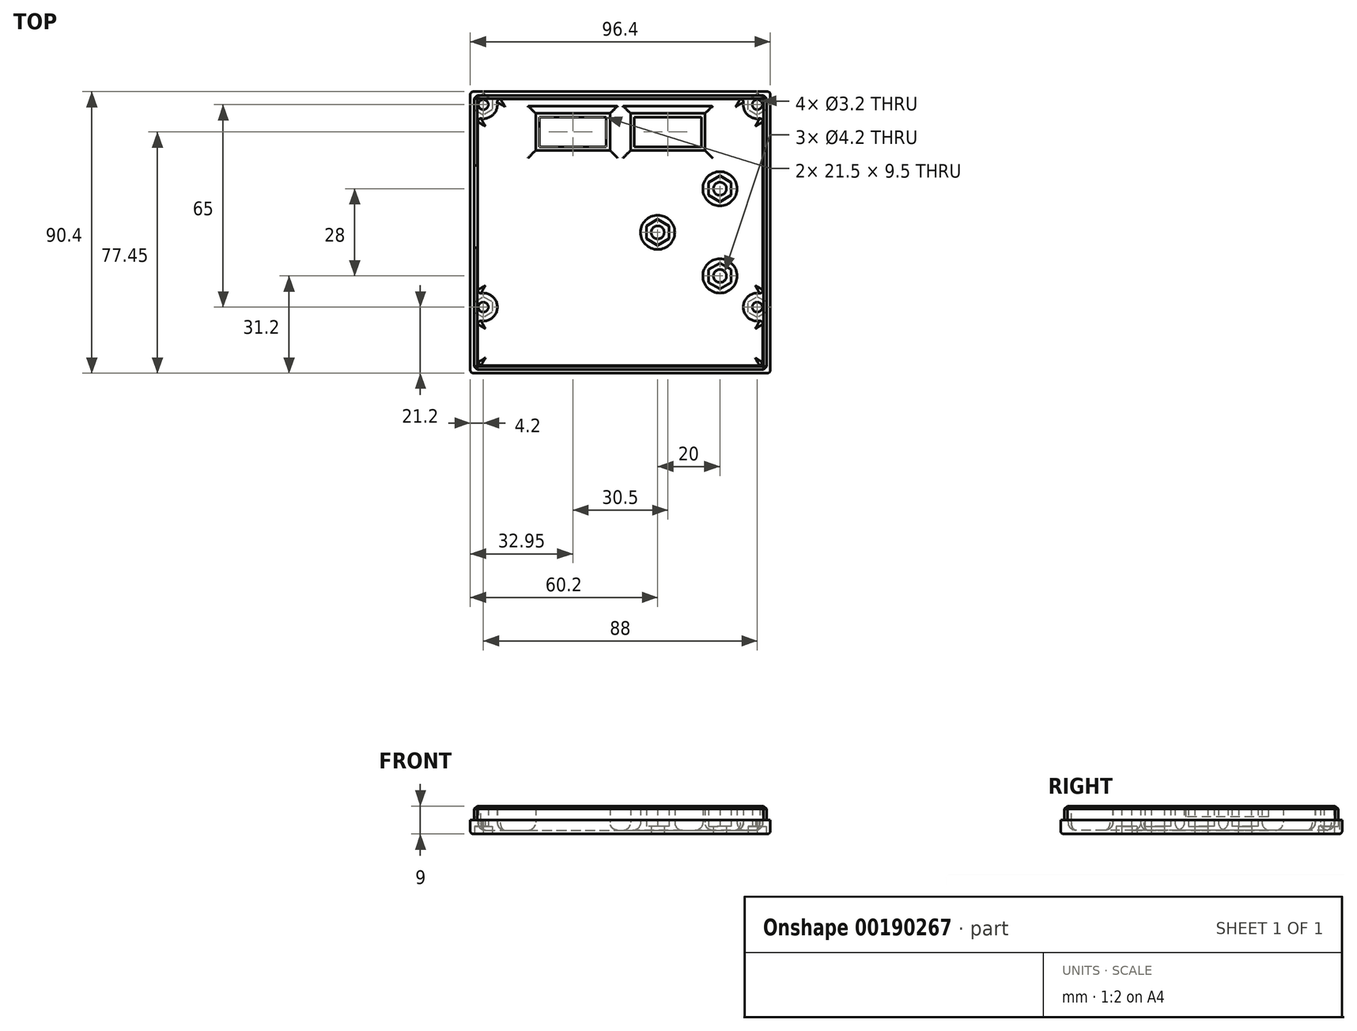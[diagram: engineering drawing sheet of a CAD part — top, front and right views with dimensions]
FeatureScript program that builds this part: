
annotation { "Feature Type Name" : "Feature", "Feature Type Description" : "" }
export const myFeature = defineFeature(function(context is Context, id is Id, definition is map)
    precondition{}
    {
        {
            var Q0;
            Q0=qCreatedBy(makeId("Top.planeOp"),FACE);
            var sketch = newSketch(context, id + "F0", { "sketchPlane" : qUnion([Q0])});
            skLineSegment(sketch, "E0.bottom", {"start": v(-47, 44) * mm, "end": v(47, 44) * mm});
            skLineSegment(sketch, "E0.top", {"start": v(-47, -44) * mm, "end": v(47, -44) * mm});
            skLineSegment(sketch, "E0.left", {"start": v(-47, 44) * mm, "end": v(-47, -44) * mm});
            skLineSegment(sketch, "E0.right", {"start": v(47, 44) * mm, "end": v(47, -44) * mm});
            skLineSegment(sketch, "E1.0", {"start": v(-48.2, 45.2) * mm, "end": v(48.2, 45.2) * mm});
            skLineSegment(sketch, "E1.1", {"start": v(-48.2, 45.2) * mm, "end": v(-48.2, -45.2) * mm});
            skLineSegment(sketch, "E1.2", {"start": v(-48.2, -45.2) * mm, "end": v(48.2, -45.2) * mm});
            skLineSegment(sketch, "E1.3", {"start": v(48.2, 45.2) * mm, "end": v(48.2, -45.2) * mm});
            skCircle(sketch, "E2", {"center": v(-44, 41) * mm, "radius": 1.6 * mm});
            skCircle(sketch, "E3", {"center": v(44, 41) * mm, "radius": 1.6 * mm});
            skCircle(sketch, "E4", {"center": v(-44, -24) * mm, "radius": 1.6 * mm});
            skCircle(sketch, "E5", {"center": v(44, -24) * mm, "radius": 1.6 * mm});
            skArc(sketch, "E6", {"start": v(-44.65, 36.55) * mm, "mid": v(-40.82, 37.82) * mm, "end": v(-39.55, 41.65) * mm});
            skArc(sketch, "E7", {"start": v(39.55, 41.65) * mm, "mid": v(40.82, 37.82) * mm, "end": v(44.65, 36.55) * mm});
            skArc(sketch, "E8", {"start": v(-44.65, -28.45) * mm, "mid": v(-39.5, -24) * mm, "end": v(-44.65, -19.55) * mm});
            skArc(sketch, "E9", {"start": v(44.65, -19.55) * mm, "mid": v(39.5, -24) * mm, "end": v(44.65, -28.45) * mm});
            skLineSegment(sketch, "E10", {"start": v(-48.2, 21.5) * mm, "end": v(-47, 21.5) * mm});
            skLineSegment(sketch, "E11", {"start": v(-48.2, -5) * mm, "end": v(-47, -5) * mm});
            skLineSegment(sketch, "E12.top", {"start": v(-45.8, -42.8) * mm, "end": v(45.8, -42.8) * mm});
            skLineSegment(sketch, "E12.left", {"start": v(-45.8, 35.56) * mm, "end": v(-45.8, -18.56) * mm});
            skLineSegment(sketch, "E12.right", {"start": v(45.8, 35.56) * mm, "end": v(45.8, -18.56) * mm});
            skLineSegment(sketch, "E13.trimOffspring", {"start": v(-45.8, -29.44) * mm, "end": v(-45.8, -42.8) * mm});
            skLineSegment(sketch, "E14.trimOffspring", {"start": v(45.8, -29.44) * mm, "end": v(45.8, -42.8) * mm});
            skArc(sketch, "E15.filletArc", {"start": v(45.8, -29.44) * mm, "mid": v(45.45, -28.68) * mm, "end": v(44.65, -28.45) * mm});
            skArc(sketch, "E16.filletArc", {"start": v(44.65, -19.55) * mm, "mid": v(45.45, -19.32) * mm, "end": v(45.8, -18.56) * mm});
            skArc(sketch, "E17.filletArc", {"start": v(-44.65, -28.45) * mm, "mid": v(-45.45, -28.68) * mm, "end": v(-45.8, -29.44) * mm});
            skArc(sketch, "E18.filletArc", {"start": v(-45.8, -18.56) * mm, "mid": v(-45.45, -19.32) * mm, "end": v(-44.65, -19.55) * mm});
            skLineSegment(sketch, "E19.trimOffspring", {"start": v(-38.56, 42.8) * mm, "end": v(38.56, 42.8) * mm});
            skArc(sketch, "E20.filletArc", {"start": v(-44.65, 36.55) * mm, "mid": v(-45.45, 36.32) * mm, "end": v(-45.8, 35.56) * mm});
            skArc(sketch, "E21.filletArc", {"start": v(-38.56, 42.8) * mm, "mid": v(-39.32, 42.45) * mm, "end": v(-39.55, 41.65) * mm});
            skPoint(sketch, "E22.visualSharp", {"position": v(39.88, 42.8) * mm});
            skArc(sketch, "E22.filletArc", {"start": v(39.55, 41.65) * mm, "mid": v(39.32, 42.45) * mm, "end": v(38.56, 42.8) * mm});
            skPoint(sketch, "E23.visualSharp", {"position": v(45.8, 36.88) * mm});
            skArc(sketch, "E23.filletArc", {"start": v(45.8, 35.56) * mm, "mid": v(45.45, 36.32) * mm, "end": v(44.65, 36.55) * mm});
            skLineSegment(sketch, "E24.bottom", {"start": v(-26, 37) * mm, "end": v(-4.5, 37) * mm});
            skLineSegment(sketch, "E24.top", {"start": v(-26, 27.5) * mm, "end": v(-4.5, 27.5) * mm});
            skLineSegment(sketch, "E24.left", {"start": v(-26, 37) * mm, "end": v(-26, 27.5) * mm});
            skLineSegment(sketch, "E24.right", {"start": v(-4.5, 37) * mm, "end": v(-4.5, 27.5) * mm});
            skLineSegment(sketch, "E25.bottom", {"start": v(4.5, 37) * mm, "end": v(26, 37) * mm});
            skLineSegment(sketch, "E25.top", {"start": v(4.5, 27.5) * mm, "end": v(26, 27.5) * mm});
            skLineSegment(sketch, "E25.left", {"start": v(4.5, 37) * mm, "end": v(4.5, 27.5) * mm});
            skLineSegment(sketch, "E25.right", {"start": v(26, 37) * mm, "end": v(26, 27.5) * mm});
            skCircle(sketch, "E26", {"center": v(32, 14) * mm, "radius": 5.5 * mm});
            skCircle(sketch, "E27", {"center": v(32, -14) * mm, "radius": 5.5 * mm});
            skCircle(sketch, "E28.cCircle", {"center": v(-44, 41) * mm, "radius": 2.9 * mm, "construction": true});
            skLineSegment(sketch, "E28.0", {"start": v(-46.9, 39.33) * mm, "end": v(-46.9, 42.67) * mm});
            skLineSegment(sketch, "E28.1", {"start": v(-46.9, 42.67) * mm, "end": v(-44, 44.35) * mm});
            skLineSegment(sketch, "E28.2", {"start": v(-44, 44.35) * mm, "end": v(-41.1, 42.67) * mm});
            skLineSegment(sketch, "E28.3", {"start": v(-41.1, 42.67) * mm, "end": v(-41.1, 39.33) * mm});
            skLineSegment(sketch, "E28.4", {"start": v(-41.1, 39.33) * mm, "end": v(-44, 37.65) * mm});
            skLineSegment(sketch, "E28.5", {"start": v(-44, 37.65) * mm, "end": v(-46.9, 39.33) * mm});
            skPoint(sketch, "E28.0.midPoint", {"position": v(-46.9, 41) * mm});
            skCircle(sketch, "E29.cCircle", {"center": v(44, 41) * mm, "radius": 2.9 * mm, "construction": true});
            skLineSegment(sketch, "E29.0", {"start": v(46.9, 42.67) * mm, "end": v(46.9, 39.33) * mm});
            skLineSegment(sketch, "E29.1", {"start": v(46.9, 39.33) * mm, "end": v(44, 37.65) * mm});
            skLineSegment(sketch, "E29.2", {"start": v(44, 37.65) * mm, "end": v(41.1, 39.33) * mm});
            skLineSegment(sketch, "E29.3", {"start": v(41.1, 39.33) * mm, "end": v(41.1, 42.67) * mm});
            skLineSegment(sketch, "E29.4", {"start": v(41.1, 42.67) * mm, "end": v(44, 44.35) * mm});
            skLineSegment(sketch, "E29.5", {"start": v(44, 44.35) * mm, "end": v(46.9, 42.67) * mm});
            skCircle(sketch, "E30.cCircle", {"center": v(-44, -24) * mm, "radius": 2.9 * mm, "construction": true});
            skLineSegment(sketch, "E30.0", {"start": v(-41.1, -22.33) * mm, "end": v(-41.1, -25.67) * mm});
            skLineSegment(sketch, "E30.1", {"start": v(-41.1, -25.67) * mm, "end": v(-44, -27.35) * mm});
            skLineSegment(sketch, "E30.2", {"start": v(-44, -27.35) * mm, "end": v(-46.9, -25.67) * mm});
            skLineSegment(sketch, "E30.3", {"start": v(-46.9, -25.67) * mm, "end": v(-46.9, -22.33) * mm});
            skLineSegment(sketch, "E30.4", {"start": v(-46.9, -22.33) * mm, "end": v(-44, -20.65) * mm});
            skLineSegment(sketch, "E30.5", {"start": v(-44, -20.65) * mm, "end": v(-41.1, -22.33) * mm});
            skPoint(sketch, "E30.0.midPoint", {"position": v(-41.1, -24) * mm});
            skCircle(sketch, "E31.cCircle", {"center": v(44, -24) * mm, "radius": 2.9 * mm, "construction": true});
            skLineSegment(sketch, "E31.0", {"start": v(46.9, -22.33) * mm, "end": v(46.9, -25.67) * mm});
            skLineSegment(sketch, "E31.1", {"start": v(46.9, -25.67) * mm, "end": v(44, -27.35) * mm});
            skLineSegment(sketch, "E31.2", {"start": v(44, -27.35) * mm, "end": v(41.1, -25.67) * mm});
            skLineSegment(sketch, "E31.3", {"start": v(41.1, -25.67) * mm, "end": v(41.1, -22.33) * mm});
            skLineSegment(sketch, "E31.4", {"start": v(41.1, -22.33) * mm, "end": v(44, -20.65) * mm});
            skLineSegment(sketch, "E31.5", {"start": v(44, -20.65) * mm, "end": v(46.9, -22.33) * mm});
            skPoint(sketch, "E31.0.midPoint", {"position": v(46.9, -24) * mm});
            skCircle(sketch, "E32.cCircle", {"center": v(32, 14) * mm, "radius": 3.6 * mm, "construction": true});
            skLineSegment(sketch, "E32.0", {"start": v(32, 9.84) * mm, "end": v(28.4, 11.92) * mm});
            skLineSegment(sketch, "E32.1", {"start": v(28.4, 11.92) * mm, "end": v(28.4, 16.08) * mm});
            skLineSegment(sketch, "E32.2", {"start": v(28.4, 16.08) * mm, "end": v(32, 18.16) * mm});
            skLineSegment(sketch, "E32.3", {"start": v(32, 18.16) * mm, "end": v(35.6, 16.08) * mm});
            skLineSegment(sketch, "E32.4", {"start": v(35.6, 16.08) * mm, "end": v(35.6, 11.92) * mm});
            skLineSegment(sketch, "E32.5", {"start": v(35.6, 11.92) * mm, "end": v(32, 9.84) * mm});
            skPoint(sketch, "E32.0.midPoint", {"position": v(30.2, 10.88) * mm});
            skCircle(sketch, "E33.cCircle", {"center": v(32, -14) * mm, "radius": 3.6 * mm, "construction": true});
            skLineSegment(sketch, "E33.0", {"start": v(28.4, -16.08) * mm, "end": v(28.4, -11.92) * mm});
            skLineSegment(sketch, "E33.1", {"start": v(28.4, -11.92) * mm, "end": v(32, -9.84) * mm});
            skLineSegment(sketch, "E33.2", {"start": v(32, -9.84) * mm, "end": v(35.6, -11.92) * mm});
            skLineSegment(sketch, "E33.3", {"start": v(35.6, -11.92) * mm, "end": v(35.6, -16.08) * mm});
            skLineSegment(sketch, "E33.4", {"start": v(35.6, -16.08) * mm, "end": v(32, -18.16) * mm});
            skLineSegment(sketch, "E33.5", {"start": v(32, -18.16) * mm, "end": v(28.4, -16.08) * mm});
            skPoint(sketch, "E33.0.midPoint", {"position": v(28.4, -14) * mm});
            skLineSegment(sketch, "E34.0", {"start": v(-27.2, 38.2) * mm, "end": v(-27.2, 26.3) * mm});
            skLineSegment(sketch, "E34.1", {"start": v(-27.2, 38.2) * mm, "end": v(-3.3, 38.2) * mm});
            skLineSegment(sketch, "E34.2", {"start": v(-3.3, 38.2) * mm, "end": v(-3.3, 26.3) * mm});
            skLineSegment(sketch, "E34.3", {"start": v(-27.2, 26.3) * mm, "end": v(-3.3, 26.3) * mm});
            skLineSegment(sketch, "E35.0", {"start": v(3.3, 38.2) * mm, "end": v(27.2, 38.2) * mm});
            skLineSegment(sketch, "E35.1", {"start": v(3.3, 38.2) * mm, "end": v(3.3, 26.3) * mm});
            skLineSegment(sketch, "E35.2", {"start": v(3.3, 26.3) * mm, "end": v(27.2, 26.3) * mm});
            skLineSegment(sketch, "E35.3", {"start": v(27.2, 38.2) * mm, "end": v(27.2, 26.3) * mm});
            skCircle(sketch, "E36", {"center": v(32, 14) * mm, "radius": 2.1 * mm});
            skCircle(sketch, "E37", {"center": v(32, -14) * mm, "radius": 2.1 * mm});
            skCircle(sketch, "E38", {"center": v(12, 0) * mm, "radius": 5.5 * mm});
            skCircle(sketch, "E39.cCircle", {"center": v(12, 0) * mm, "radius": 3.6 * mm, "construction": true});
            skLineSegment(sketch, "E39.0", {"start": v(8.4, -2.08) * mm, "end": v(8.4, 2.08) * mm});
            skLineSegment(sketch, "E39.1", {"start": v(8.4, 2.08) * mm, "end": v(12, 4.16) * mm});
            skLineSegment(sketch, "E39.2", {"start": v(12, 4.16) * mm, "end": v(15.6, 2.08) * mm});
            skLineSegment(sketch, "E39.3", {"start": v(15.6, 2.08) * mm, "end": v(15.6, -2.08) * mm});
            skLineSegment(sketch, "E39.4", {"start": v(15.6, -2.08) * mm, "end": v(12, -4.16) * mm});
            skLineSegment(sketch, "E39.5", {"start": v(12, -4.16) * mm, "end": v(8.4, -2.08) * mm});
            skPoint(sketch, "E39.0.midPoint", {"position": v(8.4, 0) * mm});
            skCircle(sketch, "E40", {"center": v(12, 0) * mm, "radius": 2.1 * mm});
            skLineSegment(sketch, "E41", {"start": v(-47, -5) * mm, "end": v(-45.8, -5) * mm});
            skLineSegment(sketch, "E42", {"start": v(-47, 21.5) * mm, "end": v(-45.8, 21.5) * mm});
            skSolve(sketch);
        }
        {
            var Q0;
            Q0=makeQuery(id+"F0.imprint","IMPRINT",FACE,{"disambiguationData":[TD([[makeQuery(id+"F0.imprint","IMPRINT",EDGE,{"derivedFrom":sQuery(id+"F0.wireOp",EDGE,"E6")}),-1.0]])]});
            var Q1;
            Q1=makeQuery(id+"F0.imprint","IMPRINT",FACE,{"disambiguationData":[TD([[makeQuery(id+"F0.imprint","IMPRINT",EDGE,{"derivedFrom":sQuery(id+"F0.wireOp",EDGE,"E25.bottom")}),1.0]])]});
            var Q2;
            Q2=makeQuery(id+"F0.imprint","IMPRINT",FACE,{"disambiguationData":[TD([[makeQuery(id+"F0.imprint","IMPRINT",EDGE,{"derivedFrom":sQuery(id+"F0.wireOp",EDGE,"E24.bottom")}),1.0]])]});
            var Q3;
            {var subQ4=sQuery(id+"F0.wireOp",EDGE,"E0.top");Q3=makeQuery(id+"F0.imprint","IMPRINT",FACE,{"disambiguationData":[TD([[makeQuery(id+"F0.imprint","IMPRINT",EDGE,{"derivedFrom":subQ4}),-1.0]])]});}
            var Q4;
            Q4=makeQuery(id+"F0.imprint","IMPRINT",FACE,{"disambiguationData":[TD([[makeQuery(id+"F0.imprint","IMPRINT",EDGE,{"derivedFrom":sQuery(id+"F0.wireOp",EDGE,"E32.0")}),-1.0]])]});
            var Q5;
            Q5=makeQuery(id+"F0.imprint","IMPRINT",FACE,{"disambiguationData":[TD([[makeQuery(id+"F0.imprint","IMPRINT",EDGE,{"derivedFrom":sQuery(id+"F0.wireOp",EDGE,"E26")}),1.0]])]});
            var Q6;
            Q6=makeQuery(id+"F0.imprint","IMPRINT",FACE,{"disambiguationData":[TD([[makeQuery(id+"F0.imprint","IMPRINT",EDGE,{"derivedFrom":sQuery(id+"F0.wireOp",EDGE,"E27")}),1.0]])]});
            var Q7;
            Q7=makeQuery(id+"F0.imprint","IMPRINT",FACE,{"disambiguationData":[TD([[makeQuery(id+"F0.imprint","IMPRINT",EDGE,{"derivedFrom":sQuery(id+"F0.wireOp",EDGE,"E33.0")}),-1.0]])]});
            var Q8;
            {var subQ14=sQuery(id+"F0.wireOp",EDGE,"E0.top");Q8=makeQuery(id+"F0.imprint","IMPRINT",FACE,{"disambiguationData":[TD([[makeQuery(id+"F0.imprint","IMPRINT",EDGE,{"derivedFrom":subQ14}),1.0]])]});}
            var Q9;
            {var subQ0=sQuery(id+"F0.wireOp",EDGE,"E10");Q9=makeQuery(id+"F0.imprint","IMPRINT",FACE,{"disambiguationData":[TD([[makeQuery(id+"F0.imprint","IMPRINT",EDGE,{"derivedFrom":subQ0}),-1.0]])]});}
            var Q10;
            Q10=makeQuery(id+"F0.imprint","IMPRINT",FACE,{"disambiguationData":[TD([[makeQuery(id+"F0.imprint","IMPRINT",EDGE,{"derivedFrom":sQuery(id+"F0.wireOp",EDGE,"E38")}),1.0]])]});
            var Q11;
            Q11=makeQuery(id+"F0.imprint","IMPRINT",FACE,{"disambiguationData":[TD([[makeQuery(id+"F0.imprint","IMPRINT",EDGE,{"derivedFrom":sQuery(id+"F0.wireOp",EDGE,"E39.0")}),-1.0]])]});
            var Q12;
            {var subQ2=sQuery(id+"F0.wireOp",EDGE,"E41");Q12=makeQuery(id+"F0.imprint","IMPRINT",FACE,{"disambiguationData":[TD([[makeQuery(id+"F0.imprint","IMPRINT",EDGE,{"derivedFrom":subQ2}),1.0]])]});}
            extrude(context, id + "F1", {"entities" : qUnion([Q0, Q1, Q2, Q3, Q4, Q5, Q6, Q7, Q8, Q9, Q10, Q11, Q12]), "depth" : 1.2 * mm});
        }
        {
            var Q0;
            Q0=makeQuery(id+"F0.imprint","IMPRINT",FACE,{"disambiguationData":[TD([[makeQuery(id+"F0.imprint","IMPRINT",EDGE,{"derivedFrom":sQuery(id+"F0.wireOp",EDGE,"E24.bottom")}),1.0]])]});
            var Q1;
            Q1=makeQuery(id+"F0.imprint","IMPRINT",FACE,{"disambiguationData":[TD([[makeQuery(id+"F0.imprint","IMPRINT",EDGE,{"derivedFrom":sQuery(id+"F0.wireOp",EDGE,"E25.bottom")}),1.0]])]});
            var Q2;
            Q2=makeQuery(id+"F0.imprint","IMPRINT",FACE,{"disambiguationData":[TD([[makeQuery(id+"F0.imprint","IMPRINT",EDGE,{"derivedFrom":sQuery(id+"F0.wireOp",EDGE,"E26")}),1.0]])]});
            var Q3;
            Q3=makeQuery(id+"F0.imprint","IMPRINT",FACE,{"disambiguationData":[TD([[makeQuery(id+"F0.imprint","IMPRINT",EDGE,{"derivedFrom":sQuery(id+"F0.wireOp",EDGE,"E38")}),1.0]])]});
            var Q4;
            Q4=makeQuery(id+"F0.imprint","IMPRINT",FACE,{"disambiguationData":[TD([[makeQuery(id+"F0.imprint","IMPRINT",EDGE,{"derivedFrom":sQuery(id+"F0.wireOp",EDGE,"E27")}),1.0]])]});
            var Q5;
            {var subQ4=sQuery(id+"F0.wireOp",EDGE,"E0.top");Q5=makeQuery(id+"F0.imprint","IMPRINT",FACE,{"disambiguationData":[TD([[makeQuery(id+"F0.imprint","IMPRINT",EDGE,{"derivedFrom":subQ4}),-1.0]])]});}
            var Q6;
            {var subQ14=sQuery(id+"F0.wireOp",EDGE,"E0.top");Q6=makeQuery(id+"F0.imprint","IMPRINT",FACE,{"disambiguationData":[TD([[makeQuery(id+"F0.imprint","IMPRINT",EDGE,{"derivedFrom":subQ14}),1.0]])]});}
            var Q7;
            {var subQ0=sQuery(id+"F0.wireOp",EDGE,"E10");Q7=makeQuery(id+"F0.imprint","IMPRINT",FACE,{"disambiguationData":[TD([[makeQuery(id+"F0.imprint","IMPRINT",EDGE,{"derivedFrom":subQ0}),-1.0]])]});}
            var Q8;
            Q8=makeQuery(id+"F0.imprint","IMPRINT",FACE,{"disambiguationData":[TD([[makeQuery(id+"F0.imprint","IMPRINT",EDGE,{"derivedFrom":sQuery(id+"F0.wireOp",EDGE,"E33.0")}),-1.0]])]});
            var Q9;
            Q9=makeQuery(id+"F0.imprint","IMPRINT",FACE,{"disambiguationData":[TD([[makeQuery(id+"F0.imprint","IMPRINT",EDGE,{"derivedFrom":sQuery(id+"F0.wireOp",EDGE,"E39.0")}),-1.0]])]});
            var Q10;
            Q10=makeQuery(id+"F0.imprint","IMPRINT",FACE,{"disambiguationData":[TD([[makeQuery(id+"F0.imprint","IMPRINT",EDGE,{"derivedFrom":sQuery(id+"F0.wireOp",EDGE,"E32.0")}),-1.0]])]});
            var Q11;
            {var subQ2=sQuery(id+"F0.wireOp",EDGE,"E41");Q11=makeQuery(id+"F0.imprint","IMPRINT",FACE,{"disambiguationData":[TD([[makeQuery(id+"F0.imprint","IMPRINT",EDGE,{"derivedFrom":subQ2}),1.0]])]});}
            extrude(context, id + "F2", {"entities" : qUnion([Q0, Q1, Q2, Q3, Q4, Q5, Q6, Q7, Q8, Q9, Q10, Q11]), "operationType" : NewBodyOperationType.ADD, "depth" : 2.5 * mm, "hasSecondDirection" : true, "secondDirectionOppositeDirection" : false, "secondDirectionDepth" : 1.2 * mm});
        }
        {
            var Q0;
            {var subQ4=sQuery(id+"F0.wireOp",EDGE,"E0.top");Q0=makeQuery(id+"F0.imprint","IMPRINT",FACE,{"disambiguationData":[TD([[makeQuery(id+"F0.imprint","IMPRINT",EDGE,{"derivedFrom":subQ4}),-1.0]])]});}
            var Q1;
            {var subQ14=sQuery(id+"F0.wireOp",EDGE,"E0.top");Q1=makeQuery(id+"F0.imprint","IMPRINT",FACE,{"disambiguationData":[TD([[makeQuery(id+"F0.imprint","IMPRINT",EDGE,{"derivedFrom":subQ14}),1.0]])]});}
            var Q2;
            Q2=makeQuery(id+"F0.imprint","IMPRINT",FACE,{"disambiguationData":[TD([[makeQuery(id+"F0.imprint","IMPRINT",EDGE,{"derivedFrom":sQuery(id+"F0.wireOp",EDGE,"E4")}),-1.0]])]});
            var Q3;
            Q3=makeQuery(id+"F0.imprint","IMPRINT",FACE,{"disambiguationData":[TD([[makeQuery(id+"F0.imprint","IMPRINT",EDGE,{"derivedFrom":sQuery(id+"F0.wireOp",EDGE,"E5")}),-1.0]])]});
            var Q4;
            Q4=makeQuery(id+"F0.imprint","IMPRINT",FACE,{"disambiguationData":[TD([[makeQuery(id+"F0.imprint","IMPRINT",EDGE,{"derivedFrom":sQuery(id+"F0.wireOp",EDGE,"E3")}),-1.0]])]});
            var Q5;
            Q5=makeQuery(id+"F0.imprint","IMPRINT",FACE,{"disambiguationData":[TD([[makeQuery(id+"F0.imprint","IMPRINT",EDGE,{"derivedFrom":sQuery(id+"F0.wireOp",EDGE,"E2")}),-1.0]])]});
            var Q6;
            Q6=makeQuery(id+"F0.imprint","IMPRINT",FACE,{"disambiguationData":[TD([[makeQuery(id+"F0.imprint","IMPRINT",EDGE,{"derivedFrom":sQuery(id+"F0.wireOp",EDGE,"E24.bottom")}),1.0]])]});
            var Q7;
            Q7=makeQuery(id+"F0.imprint","IMPRINT",FACE,{"disambiguationData":[TD([[makeQuery(id+"F0.imprint","IMPRINT",EDGE,{"derivedFrom":sQuery(id+"F0.wireOp",EDGE,"E25.bottom")}),1.0]])]});
            var Q8;
            Q8=makeQuery(id+"F0.imprint","IMPRINT",FACE,{"disambiguationData":[TD([[makeQuery(id+"F0.imprint","IMPRINT",EDGE,{"derivedFrom":sQuery(id+"F0.wireOp",EDGE,"E38")}),1.0]])]});
            var Q9;
            Q9=makeQuery(id+"F0.imprint","IMPRINT",FACE,{"disambiguationData":[TD([[makeQuery(id+"F0.imprint","IMPRINT",EDGE,{"derivedFrom":sQuery(id+"F0.wireOp",EDGE,"E27")}),1.0]])]});
            var Q10;
            Q10=makeQuery(id+"F0.imprint","IMPRINT",FACE,{"disambiguationData":[TD([[makeQuery(id+"F0.imprint","IMPRINT",EDGE,{"derivedFrom":sQuery(id+"F0.wireOp",EDGE,"E26")}),1.0]])]});
            var Q11;
            {var subQ0=sQuery(id+"F0.wireOp",EDGE,"E10");Q11=makeQuery(id+"F0.imprint","IMPRINT",FACE,{"disambiguationData":[TD([[makeQuery(id+"F0.imprint","IMPRINT",EDGE,{"derivedFrom":subQ0}),-1.0]])]});}
            var Q12;
            {var subQ2=sQuery(id+"F0.wireOp",EDGE,"E41");Q12=makeQuery(id+"F0.imprint","IMPRINT",FACE,{"disambiguationData":[TD([[makeQuery(id+"F0.imprint","IMPRINT",EDGE,{"derivedFrom":subQ2}),1.0]])]});}
            var Q13;
            Q13=makeQuery(id+"F1.opExtrude","SWEPT_BODY",BODY,{"disambiguationData":[OSD([sQuery(id+"F0.wireOp",EDGE,"E1.0"),sQuery(id+"F0.wireOp",EDGE,"E1.1"),sQuery(id+"F0.wireOp",EDGE,"E1.2"),sQuery(id+"F0.wireOp",EDGE,"E1.3"),sQuery(id+"F0.wireOp",EDGE,"E24.bottom"),sQuery(id+"F0.wireOp",EDGE,"E24.top"),sQuery(id+"F0.wireOp",EDGE,"E24.left"),sQuery(id+"F0.wireOp",EDGE,"E24.right"),sQuery(id+"F0.wireOp",EDGE,"E25.bottom"),sQuery(id+"F0.wireOp",EDGE,"E25.top"),sQuery(id+"F0.wireOp",EDGE,"E25.left"),sQuery(id+"F0.wireOp",EDGE,"E25.right"),sQuery(id+"F0.wireOp",EDGE,"E28.0"),sQuery(id+"F0.wireOp",EDGE,"E28.1"),sQuery(id+"F0.wireOp",EDGE,"E28.2"),sQuery(id+"F0.wireOp",EDGE,"E28.3"),sQuery(id+"F0.wireOp",EDGE,"E28.4"),sQuery(id+"F0.wireOp",EDGE,"E28.5"),sQuery(id+"F0.wireOp",EDGE,"E29.0"),sQuery(id+"F0.wireOp",EDGE,"E29.1"),sQuery(id+"F0.wireOp",EDGE,"E29.2"),sQuery(id+"F0.wireOp",EDGE,"E29.3"),sQuery(id+"F0.wireOp",EDGE,"E29.4"),sQuery(id+"F0.wireOp",EDGE,"E29.5"),sQuery(id+"F0.wireOp",EDGE,"E30.0"),sQuery(id+"F0.wireOp",EDGE,"E30.1"),sQuery(id+"F0.wireOp",EDGE,"E30.2"),sQuery(id+"F0.wireOp",EDGE,"E30.3"),sQuery(id+"F0.wireOp",EDGE,"E30.4"),sQuery(id+"F0.wireOp",EDGE,"E30.5"),sQuery(id+"F0.wireOp",EDGE,"E31.0"),sQuery(id+"F0.wireOp",EDGE,"E31.1"),sQuery(id+"F0.wireOp",EDGE,"E31.2"),sQuery(id+"F0.wireOp",EDGE,"E31.3"),sQuery(id+"F0.wireOp",EDGE,"E31.4"),sQuery(id+"F0.wireOp",EDGE,"E31.5"),sQuery(id+"F0.wireOp",EDGE,"E36"),sQuery(id+"F0.wireOp",EDGE,"E37"),sQuery(id+"F0.wireOp",EDGE,"E40")])]});
            extrude(context, id + "F3", {"entities" : qUnion([Q0, Q1, Q2, Q3, Q4, Q5, Q6, Q7, Q8, Q9, Q10, Q11, Q12]), "operationType" : NewBodyOperationType.ADD, "depth" : 4.5 * mm, "hasSecondDirection" : true, "secondDirectionOppositeDirection" : false, "secondDirectionBoundEntityBody" : qUnion([Q13]), "secondDirectionDepth" : 2.5 * mm});
        }
        {
            var Q0;
            Q0=makeQuery(id+"F0.imprint","IMPRINT",FACE,{"disambiguationData":[TD([[makeQuery(id+"F0.imprint","IMPRINT",EDGE,{"derivedFrom":sQuery(id+"F0.wireOp",EDGE,"E24.bottom")}),1.0]])]});
            var Q1;
            Q1=makeQuery(id+"F0.imprint","IMPRINT",FACE,{"disambiguationData":[TD([[makeQuery(id+"F0.imprint","IMPRINT",EDGE,{"derivedFrom":sQuery(id+"F0.wireOp",EDGE,"E25.bottom")}),1.0]])]});
            var Q2;
            {var subQ14=sQuery(id+"F0.wireOp",EDGE,"E0.top");Q2=makeQuery(id+"F0.imprint","IMPRINT",FACE,{"disambiguationData":[TD([[makeQuery(id+"F0.imprint","IMPRINT",EDGE,{"derivedFrom":subQ14}),1.0]])]});}
            var Q3;
            Q3=makeQuery(id+"F0.imprint","IMPRINT",FACE,{"disambiguationData":[TD([[makeQuery(id+"F0.imprint","IMPRINT",EDGE,{"derivedFrom":sQuery(id+"F0.wireOp",EDGE,"E38")}),1.0]])]});
            var Q4;
            Q4=makeQuery(id+"F0.imprint","IMPRINT",FACE,{"disambiguationData":[TD([[makeQuery(id+"F0.imprint","IMPRINT",EDGE,{"derivedFrom":sQuery(id+"F0.wireOp",EDGE,"E27")}),1.0]])]});
            var Q5;
            Q5=makeQuery(id+"F0.imprint","IMPRINT",FACE,{"disambiguationData":[TD([[makeQuery(id+"F0.imprint","IMPRINT",EDGE,{"derivedFrom":sQuery(id+"F0.wireOp",EDGE,"E26")}),1.0]])]});
            var Q6;
            Q6=makeQuery(id+"F0.imprint","IMPRINT",FACE,{"disambiguationData":[TD([[makeQuery(id+"F0.imprint","IMPRINT",EDGE,{"derivedFrom":sQuery(id+"F0.wireOp",EDGE,"E4")}),-1.0]])]});
            var Q7;
            Q7=makeQuery(id+"F0.imprint","IMPRINT",FACE,{"disambiguationData":[TD([[makeQuery(id+"F0.imprint","IMPRINT",EDGE,{"derivedFrom":sQuery(id+"F0.wireOp",EDGE,"E5")}),-1.0]])]});
            var Q8;
            Q8=makeQuery(id+"F0.imprint","IMPRINT",FACE,{"disambiguationData":[TD([[makeQuery(id+"F0.imprint","IMPRINT",EDGE,{"derivedFrom":sQuery(id+"F0.wireOp",EDGE,"E3")}),-1.0]])]});
            var Q9;
            Q9=makeQuery(id+"F0.imprint","IMPRINT",FACE,{"disambiguationData":[TD([[makeQuery(id+"F0.imprint","IMPRINT",EDGE,{"derivedFrom":sQuery(id+"F0.wireOp",EDGE,"E2")}),-1.0]])]});
            var Q10;
            {var subQ2=sQuery(id+"F0.wireOp",EDGE,"E41");Q10=makeQuery(id+"F0.imprint","IMPRINT",FACE,{"disambiguationData":[TD([[makeQuery(id+"F0.imprint","IMPRINT",EDGE,{"derivedFrom":subQ2}),1.0]])]});}
            extrude(context, id + "F4", {"entities" : qUnion([Q0, Q1, Q2, Q3, Q4, Q5, Q6, Q7, Q8, Q9, Q10]), "operationType" : NewBodyOperationType.ADD, "depth" : 5.5 * mm, "hasSecondDirection" : true, "secondDirectionOppositeDirection" : false, "secondDirectionDepth" : 4.5 * mm});
        }
        {
            var Q0;
            {var subQ15=sQuery(id+"F0.wireOp",EDGE,"E0.top");Q0=makeQuery(id+"F0.imprint","IMPRINT",FACE,{"disambiguationData":[TD([[makeQuery(id+"F0.imprint","IMPRINT",EDGE,{"derivedFrom":subQ15}),1.0]])]});}
            var Q1;
            Q1=makeQuery(id+"F0.imprint","IMPRINT",FACE,{"disambiguationData":[TD([[makeQuery(id+"F0.imprint","IMPRINT",EDGE,{"derivedFrom":sQuery(id+"F0.wireOp",EDGE,"E2")}),-1.0]])]});
            var Q2;
            Q2=makeQuery(id+"F0.imprint","IMPRINT",FACE,{"disambiguationData":[TD([[makeQuery(id+"F0.imprint","IMPRINT",EDGE,{"derivedFrom":sQuery(id+"F0.wireOp",EDGE,"E3")}),-1.0]])]});
            var Q3;
            Q3=makeQuery(id+"F0.imprint","IMPRINT",FACE,{"disambiguationData":[TD([[makeQuery(id+"F0.imprint","IMPRINT",EDGE,{"derivedFrom":sQuery(id+"F0.wireOp",EDGE,"E5")}),-1.0]])]});
            var Q4;
            Q4=makeQuery(id+"F0.imprint","IMPRINT",FACE,{"disambiguationData":[TD([[makeQuery(id+"F0.imprint","IMPRINT",EDGE,{"derivedFrom":sQuery(id+"F0.wireOp",EDGE,"E38")}),1.0]])]});
            var Q5;
            Q5=makeQuery(id+"F0.imprint","IMPRINT",FACE,{"disambiguationData":[TD([[makeQuery(id+"F0.imprint","IMPRINT",EDGE,{"derivedFrom":sQuery(id+"F0.wireOp",EDGE,"E27")}),1.0]])]});
            var Q6;
            Q6=makeQuery(id+"F0.imprint","IMPRINT",FACE,{"disambiguationData":[TD([[makeQuery(id+"F0.imprint","IMPRINT",EDGE,{"derivedFrom":sQuery(id+"F0.wireOp",EDGE,"E26")}),1.0]])]});
            var Q7;
            Q7=makeQuery(id+"F0.imprint","IMPRINT",FACE,{"disambiguationData":[TD([[makeQuery(id+"F0.imprint","IMPRINT",EDGE,{"derivedFrom":sQuery(id+"F0.wireOp",EDGE,"E25.bottom")}),1.0]])]});
            var Q8;
            Q8=makeQuery(id+"F0.imprint","IMPRINT",FACE,{"disambiguationData":[TD([[makeQuery(id+"F0.imprint","IMPRINT",EDGE,{"derivedFrom":sQuery(id+"F0.wireOp",EDGE,"E24.bottom")}),1.0]])]});
            var Q9;
            Q9=makeQuery(id+"F0.imprint","IMPRINT",FACE,{"disambiguationData":[TD([[makeQuery(id+"F0.imprint","IMPRINT",EDGE,{"derivedFrom":sQuery(id+"F0.wireOp",EDGE,"E4")}),-1.0]])]});
            extrude(context, id + "F5", {"entities" : qUnion([Q0, Q1, Q2, Q3, Q4, Q5, Q6, Q7, Q8, Q9]), "operationType" : NewBodyOperationType.ADD, "depth" : 9 * mm, "hasSecondDirection" : true, "secondDirectionOppositeDirection" : false, "secondDirectionDepth" : 5.5 * mm});
        }
        {
            var Q0;
            Q0=makeQuery(id+"F1.opExtrude","CAP_FACE",FACE,{"disambiguationData":[OSD([sQuery(id+"F0.wireOp",EDGE,"E1.0"),sQuery(id+"F0.wireOp",EDGE,"E1.1"),sQuery(id+"F0.wireOp",EDGE,"E1.2"),sQuery(id+"F0.wireOp",EDGE,"E1.3"),sQuery(id+"F0.wireOp",EDGE,"E24.bottom"),sQuery(id+"F0.wireOp",EDGE,"E24.top"),sQuery(id+"F0.wireOp",EDGE,"E24.left"),sQuery(id+"F0.wireOp",EDGE,"E24.right"),sQuery(id+"F0.wireOp",EDGE,"E25.bottom"),sQuery(id+"F0.wireOp",EDGE,"E25.top"),sQuery(id+"F0.wireOp",EDGE,"E25.left"),sQuery(id+"F0.wireOp",EDGE,"E25.right"),sQuery(id+"F0.wireOp",EDGE,"E28.0"),sQuery(id+"F0.wireOp",EDGE,"E28.1"),sQuery(id+"F0.wireOp",EDGE,"E28.2"),sQuery(id+"F0.wireOp",EDGE,"E28.3"),sQuery(id+"F0.wireOp",EDGE,"E28.4"),sQuery(id+"F0.wireOp",EDGE,"E28.5"),sQuery(id+"F0.wireOp",EDGE,"E29.0"),sQuery(id+"F0.wireOp",EDGE,"E29.1"),sQuery(id+"F0.wireOp",EDGE,"E29.2"),sQuery(id+"F0.wireOp",EDGE,"E29.3"),sQuery(id+"F0.wireOp",EDGE,"E29.4"),sQuery(id+"F0.wireOp",EDGE,"E29.5"),sQuery(id+"F0.wireOp",EDGE,"E30.0"),sQuery(id+"F0.wireOp",EDGE,"E30.1"),sQuery(id+"F0.wireOp",EDGE,"E30.2"),sQuery(id+"F0.wireOp",EDGE,"E30.3"),sQuery(id+"F0.wireOp",EDGE,"E30.4"),sQuery(id+"F0.wireOp",EDGE,"E30.5"),sQuery(id+"F0.wireOp",EDGE,"E31.0"),sQuery(id+"F0.wireOp",EDGE,"E31.1"),sQuery(id+"F0.wireOp",EDGE,"E31.2"),sQuery(id+"F0.wireOp",EDGE,"E31.3"),sQuery(id+"F0.wireOp",EDGE,"E31.4"),sQuery(id+"F0.wireOp",EDGE,"E31.5"),sQuery(id+"F0.wireOp",EDGE,"E36"),sQuery(id+"F0.wireOp",EDGE,"E37"),sQuery(id+"F0.wireOp",EDGE,"E40")])],"isStart":false});
            fillet(context, id + "F6", {"entities" : qUnion([Q0]), "radius" : 2.5 * mm, "tangentPropagation" : true, "allowEdgeOverflow" : false});
        }
        {
            var Q0;
            Q0=makeQuery(id+"F5.opExtrude","CAP_EDGE",EDGE,{"disambiguationData":[OSD([sQuery(id+"F0.wireOp",EDGE,"E0.bottom")])],"isStart":false});
            var Q1;
            {var subQ0=sQuery(id+"F0.wireOp",EDGE,"E0.left");Q1=makeQuery(id+"F5.opExtrude","CAP_EDGE",EDGE,{"disambiguationData":[OSD([subQ0]),TDD([makeQuery(id+"F0.imprint","IMPRINT",EDGE,{"disambiguationData":[TD([[makeQuery(id+"F0.imprint","INTERSECT",VERTEX,{"derivedFrom":[sQuery(id+"F0.wireOp",EDGE,"E0.bottom"),subQ0]}),-1.0]])],"derivedFrom":subQ0})])],"isStart":false});}
            var Q2;
            {var subQ0=sQuery(id+"F0.wireOp",EDGE,"E0.left");Q2=makeQuery(id+"F5.opExtrude","CAP_EDGE",EDGE,{"disambiguationData":[OSD([subQ0]),TDD([makeQuery(id+"F0.imprint","IMPRINT",EDGE,{"disambiguationData":[TD([[makeQuery(id+"F0.imprint","INTERSECT",VERTEX,{"derivedFrom":[sQuery(id+"F0.wireOp",EDGE,"E0.top"),subQ0]}),1.0]])],"derivedFrom":subQ0})])],"isStart":false});}
            var Q3;
            Q3=makeQuery(id+"F5.opExtrude","CAP_EDGE",EDGE,{"disambiguationData":[OSD([sQuery(id+"F0.wireOp",EDGE,"E0.top")])],"isStart":false});
            var Q4;
            Q4=makeQuery(id+"F5.opExtrude","CAP_EDGE",EDGE,{"disambiguationData":[OSD([sQuery(id+"F0.wireOp",EDGE,"E0.right")])],"isStart":false});
            var Q5;
            {var subQ0=sQuery(id+"F0.wireOp",EDGE,"E0.left");var subQ1=sQuery(id+"F0.wireOp",EDGE,"E0.top");Q5=makeQuery(id+"F5.boolean.opBoolean","MERGE",EDGE,{"derivedFrom":[makeQuery(id+"F4.opExtrude","SWEPT_EDGE",EDGE,{"disambiguationData":[OSD([subQ1,subQ0])]}),makeQuery(id+"F5.opExtrude","SWEPT_EDGE",EDGE,{"disambiguationData":[OSD([subQ1,subQ0])]})]});}
            var Q6;
            {var subQ0=sQuery(id+"F0.wireOp",EDGE,"E0.right");var subQ1=sQuery(id+"F0.wireOp",EDGE,"E0.top");Q6=makeQuery(id+"F5.boolean.opBoolean","MERGE",EDGE,{"derivedFrom":[makeQuery(id+"F4.opExtrude","SWEPT_EDGE",EDGE,{"disambiguationData":[OSD([subQ1,subQ0])]}),makeQuery(id+"F5.opExtrude","SWEPT_EDGE",EDGE,{"disambiguationData":[OSD([subQ1,subQ0])]})]});}
            var Q7;
            {var subQ0=sQuery(id+"F0.wireOp",EDGE,"E0.right");var subQ1=sQuery(id+"F0.wireOp",EDGE,"E0.bottom");Q7=makeQuery(id+"F5.boolean.opBoolean","MERGE",EDGE,{"derivedFrom":[makeQuery(id+"F4.opExtrude","SWEPT_EDGE",EDGE,{"disambiguationData":[OSD([subQ1,subQ0])]}),makeQuery(id+"F5.opExtrude","SWEPT_EDGE",EDGE,{"disambiguationData":[OSD([subQ1,subQ0])]})]});}
            var Q8;
            {var subQ0=sQuery(id+"F0.wireOp",EDGE,"E0.left");var subQ1=sQuery(id+"F0.wireOp",EDGE,"E0.bottom");Q8=makeQuery(id+"F5.boolean.opBoolean","MERGE",EDGE,{"derivedFrom":[makeQuery(id+"F4.opExtrude","SWEPT_EDGE",EDGE,{"disambiguationData":[OSD([subQ1,subQ0])]}),makeQuery(id+"F5.opExtrude","SWEPT_EDGE",EDGE,{"disambiguationData":[OSD([subQ1,subQ0])]})]});}
            var Q9;
            {var subQ0=sQuery(id+"F0.wireOp",EDGE,"E14.trimOffspring");var subQ1=sQuery(id+"F0.wireOp",EDGE,"E12.top");Q9=makeQuery(id+"F5.boolean.opBoolean","MERGE",EDGE,{"derivedFrom":[makeQuery(id+"F4.boolean.opBoolean","MERGE",EDGE,{"derivedFrom":[makeQuery(id+"F3.boolean.opBoolean","MERGE",EDGE,{"derivedFrom":[makeQuery(id+"F2.opExtrude","SWEPT_EDGE",EDGE,{"disambiguationData":[OSD([subQ1,subQ0])]}),makeQuery(id+"F3.opExtrude","SWEPT_EDGE",EDGE,{"disambiguationData":[OSD([subQ1,subQ0])]})]}),makeQuery(id+"F4.opExtrude","SWEPT_EDGE",EDGE,{"disambiguationData":[OSD([subQ1,subQ0])]})]}),makeQuery(id+"F5.opExtrude","SWEPT_EDGE",EDGE,{"disambiguationData":[OSD([subQ1,subQ0])]})]});}
            var Q10;
            {var subQ0=sQuery(id+"F0.wireOp",EDGE,"E13.trimOffspring");var subQ1=sQuery(id+"F0.wireOp",EDGE,"E12.top");Q10=makeQuery(id+"F5.boolean.opBoolean","MERGE",EDGE,{"derivedFrom":[makeQuery(id+"F4.boolean.opBoolean","MERGE",EDGE,{"derivedFrom":[makeQuery(id+"F3.boolean.opBoolean","MERGE",EDGE,{"derivedFrom":[makeQuery(id+"F2.opExtrude","SWEPT_EDGE",EDGE,{"disambiguationData":[OSD([subQ1,subQ0])]}),makeQuery(id+"F3.opExtrude","SWEPT_EDGE",EDGE,{"disambiguationData":[OSD([subQ1,subQ0])]})]}),makeQuery(id+"F4.opExtrude","SWEPT_EDGE",EDGE,{"disambiguationData":[OSD([subQ1,subQ0])]})]}),makeQuery(id+"F5.opExtrude","SWEPT_EDGE",EDGE,{"disambiguationData":[OSD([subQ1,subQ0])]})]});}
            chamfer(context, id + "F7", {"entities" : qUnion([Q0, Q1, Q2, Q3, Q4, Q5, Q6, Q7, Q8, Q9, Q10]), "width" : 1 * mm, "tangentPropagation" : true});
        }
        {
            var Q0;
            {var subQ0=sQuery(id+"F0.wireOp",EDGE,"E1.3");var subQ1=sQuery(id+"F0.wireOp",EDGE,"E1.0");Q0=makeQuery(id+"F3.boolean.opBoolean","MERGE",EDGE,{"derivedFrom":[makeQuery(id+"F2.boolean.opBoolean","MERGE",EDGE,{"derivedFrom":[makeQuery(id+"F1.opExtrude","SWEPT_EDGE",EDGE,{"disambiguationData":[OSD([subQ1,subQ0])]}),makeQuery(id+"F2.opExtrude","SWEPT_EDGE",EDGE,{"disambiguationData":[OSD([subQ1,subQ0])]})]}),makeQuery(id+"F3.opExtrude","SWEPT_EDGE",EDGE,{"disambiguationData":[OSD([subQ1,subQ0])]})]});}
            var Q1;
            Q1=makeQuery(id+"F1.opExtrude","CAP_EDGE",EDGE,{"disambiguationData":[OSD([sQuery(id+"F0.wireOp",EDGE,"E1.0")])],"isStart":true});
            var Q2;
            {var subQ0=sQuery(id+"F0.wireOp",EDGE,"E1.1");var subQ1=sQuery(id+"F0.wireOp",EDGE,"E1.0");Q2=makeQuery(id+"F3.boolean.opBoolean","MERGE",EDGE,{"derivedFrom":[makeQuery(id+"F2.boolean.opBoolean","MERGE",EDGE,{"derivedFrom":[makeQuery(id+"F1.opExtrude","SWEPT_EDGE",EDGE,{"disambiguationData":[OSD([subQ1,subQ0])]}),makeQuery(id+"F2.opExtrude","SWEPT_EDGE",EDGE,{"disambiguationData":[OSD([subQ1,subQ0])]})]}),makeQuery(id+"F3.opExtrude","SWEPT_EDGE",EDGE,{"disambiguationData":[OSD([subQ1,subQ0])]})]});}
            var Q3;
            Q3=makeQuery(id+"F1.opExtrude","CAP_EDGE",EDGE,{"disambiguationData":[OSD([sQuery(id+"F0.wireOp",EDGE,"E1.1")])],"isStart":true});
            var Q4;
            {var subQ0=sQuery(id+"F0.wireOp",EDGE,"E1.2");var subQ1=sQuery(id+"F0.wireOp",EDGE,"E1.1");Q4=makeQuery(id+"F3.boolean.opBoolean","MERGE",EDGE,{"derivedFrom":[makeQuery(id+"F2.boolean.opBoolean","MERGE",EDGE,{"derivedFrom":[makeQuery(id+"F1.opExtrude","SWEPT_EDGE",EDGE,{"disambiguationData":[OSD([subQ1,subQ0])]}),makeQuery(id+"F2.opExtrude","SWEPT_EDGE",EDGE,{"disambiguationData":[OSD([subQ1,subQ0])]})]}),makeQuery(id+"F3.opExtrude","SWEPT_EDGE",EDGE,{"disambiguationData":[OSD([subQ1,subQ0])]})]});}
            var Q5;
            Q5=makeQuery(id+"F1.opExtrude","CAP_EDGE",EDGE,{"disambiguationData":[OSD([sQuery(id+"F0.wireOp",EDGE,"E1.2")])],"isStart":true});
            var Q6;
            {var subQ0=sQuery(id+"F0.wireOp",EDGE,"E1.3");var subQ1=sQuery(id+"F0.wireOp",EDGE,"E1.2");Q6=makeQuery(id+"F3.boolean.opBoolean","MERGE",EDGE,{"derivedFrom":[makeQuery(id+"F2.boolean.opBoolean","MERGE",EDGE,{"derivedFrom":[makeQuery(id+"F1.opExtrude","SWEPT_EDGE",EDGE,{"disambiguationData":[OSD([subQ1,subQ0])]}),makeQuery(id+"F2.opExtrude","SWEPT_EDGE",EDGE,{"disambiguationData":[OSD([subQ1,subQ0])]})]}),makeQuery(id+"F3.opExtrude","SWEPT_EDGE",EDGE,{"disambiguationData":[OSD([subQ1,subQ0])]})]});}
            var Q7;
            Q7=makeQuery(id+"F1.opExtrude","CAP_EDGE",EDGE,{"disambiguationData":[OSD([sQuery(id+"F0.wireOp",EDGE,"E1.3")])],"isStart":true});
            fillet(context, id + "F8", {"entities" : qUnion([Q0, Q1, Q2, Q3, Q4, Q5, Q6, Q7]), "radius" : 1 * mm, "tangentPropagation" : true, "allowEdgeOverflow" : false});
        }
    });
